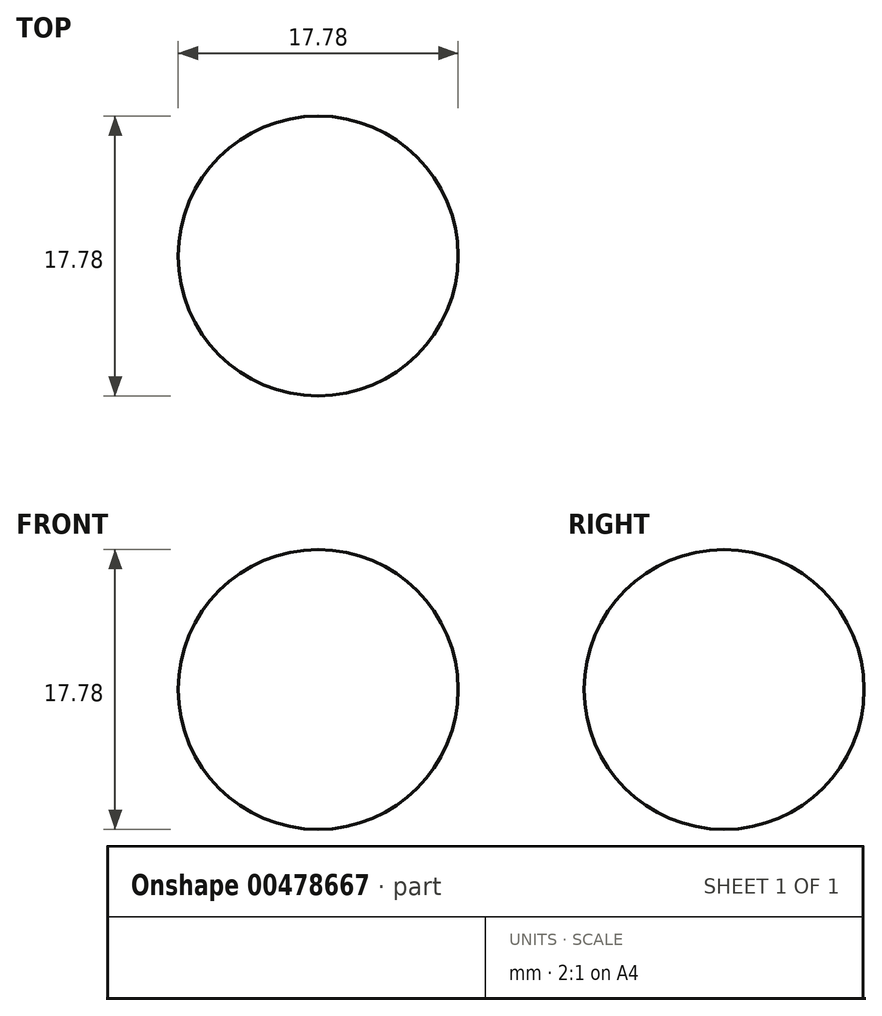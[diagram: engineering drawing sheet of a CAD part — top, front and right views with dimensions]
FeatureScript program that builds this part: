
annotation { "Feature Type Name" : "Feature", "Feature Type Description" : "" }
export const myFeature = defineFeature(function(context is Context, id is Id, definition is map)
    precondition{}
    {
        {
            var Q0;
            Q0=qCreatedBy(makeId("Front.planeOp"),FACE);
            var sketch = newSketch(context, id + "F0", { "sketchPlane" : qUnion([Q0])});
            skArc(sketch, "E0", {"start": v(0, 8.9) * mm, "mid": v(-8.9, 0) * mm, "end": v(0, -8.9) * mm});
            skLineSegment(sketch, "E1", {"start": v(0, 8.9) * mm, "end": v(0, -8.9) * mm});
            skSolve(sketch);
        }
        {
            var Q0;
            Q0=makeQuery(id+"F0.imprint","IMPRINT",FACE,{"disambiguationData":[TD([[makeQuery(id+"F0.imprint","IMPRINT",EDGE,{"derivedFrom":sQuery(id+"F0.wireOp",EDGE,"E0")}),1.0]])]});
            var Q1;
            Q1=sQuery(id+"F0.wireOp",EDGE,"E1");
            revolve(context, id + "F1", {"entities" : qUnion([Q0]), "axis" : qUnion([Q1]), "revolveType" : RevolveType.FULL});
        }
    });
